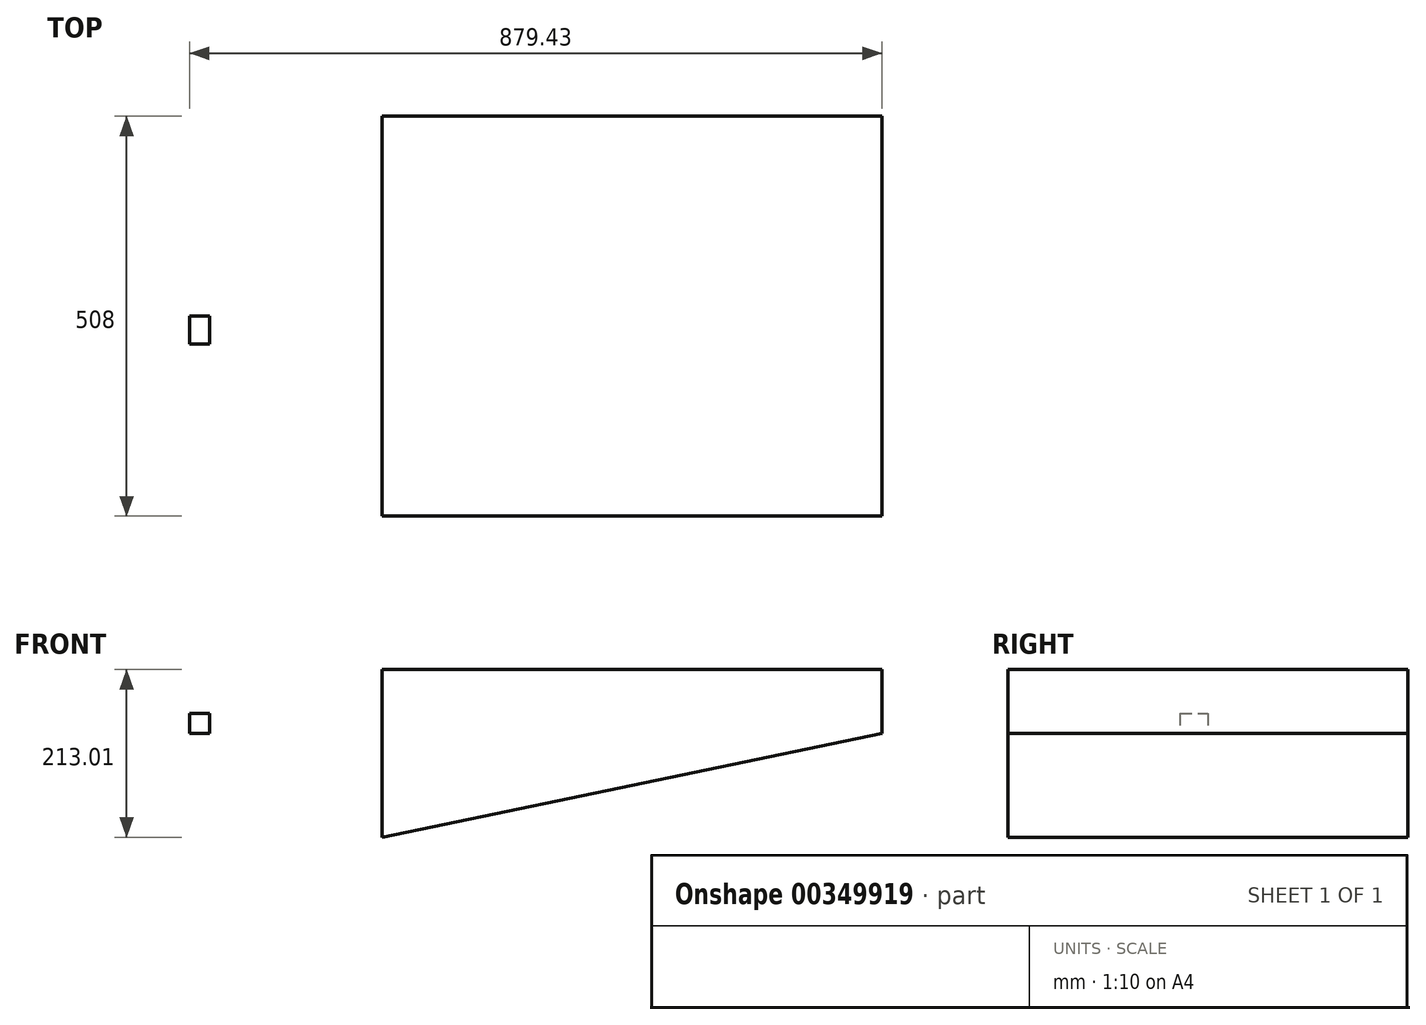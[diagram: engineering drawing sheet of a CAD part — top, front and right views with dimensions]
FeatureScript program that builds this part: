
annotation { "Feature Type Name" : "Feature", "Feature Type Description" : "" }
export const myFeature = defineFeature(function(context is Context, id is Id, definition is map)
    precondition{}
    {
        {
            var Q0;
            Q0=qCreatedBy(makeId("Top.planeOp"),FACE);
            var sketch = newSketch(context, id + "F0", { "sketchPlane" : qUnion([Q0])});
            skLineSegment(sketch, "E0.bottom", {"start": v(317.5, -254) * mm, "end": v(-317.5, -254) * mm});
            skLineSegment(sketch, "E0.top", {"start": v(317.5, 254) * mm, "end": v(-317.5, 254) * mm});
            skLineSegment(sketch, "E0.left", {"start": v(317.5, -254) * mm, "end": v(317.5, 254) * mm});
            skLineSegment(sketch, "E0.right", {"start": v(-317.5, -254) * mm, "end": v(-317.5, 254) * mm});
            skPoint(sketch, "E0.middle", {"position": v(0, 0) * mm});
            skSolve(sketch);
        }
        {
            var Q0;
            Q0 = qSketchRegion(id + "F0", true);
            extrude(context, id + "F1", {"entities" : qUnion([Q0]), "depth" : 81.28 * mm, "offsetDistance" : 25.4 * mm});
        }
        {
            var Q0;
            Q0=makeQuery(id+"F1.opExtrude","SWEPT_FACE",FACE,{"disambiguationData":[OSD([sQuery(id+"F0.wireOp",EDGE,"E0.bottom")])]});
            var sketch = newSketch(context, id + "F2", { "sketchPlane" : qUnion([Q0])});
            skLineSegment(sketch, "E1", {"start": v(-317.5, 26.86) * mm, "end": v(-317.5, -131.73) * mm});
            skLineSegment(sketch, "E2", {"start": v(-317.5, -131.73) * mm, "end": v(317.5, 0) * mm});
            skLineSegment(sketch, "E3", {"start": v(317.5, 0) * mm, "end": v(317.5, 19.8) * mm});
            skLineSegment(sketch, "E4", {"start": v(317.5, 19.8) * mm, "end": v(-317.5, 26.86) * mm});
            skSolve(sketch);
        }
        {
            var Q0;
            Q0 = qSketchRegion(id + "F2", true);
            extrude(context, id + "F3", {"entities" : qUnion([Q0]), "operationType" : NewBodyOperationType.ADD, "oppositeDirection" : true, "depth" : 508 * mm, "offsetDistance" : 25.4 * mm});
        }
        {
            var Q0;
            Q0=qCreatedBy(makeId("Front.planeOp"),FACE);
            var sketch = newSketch(context, id + "F4", { "sketchPlane" : qUnion([Q0])});
            skLineSegment(sketch, "E5.bottom", {"start": v(-561.93, 25.4) * mm, "end": v(-536.53, 25.4) * mm});
            skLineSegment(sketch, "E5.top", {"start": v(-561.93, 0) * mm, "end": v(-536.53, 0) * mm});
            skLineSegment(sketch, "E5.left", {"start": v(-561.93, 25.4) * mm, "end": v(-561.93, 0) * mm});
            skLineSegment(sketch, "E5.right", {"start": v(-536.53, 25.4) * mm, "end": v(-536.53, 0) * mm});
            skSolve(sketch);
        }
        {
            var Q0;
            Q0 = qSketchRegion(id + "F4", true);
            extrude(context, id + "F5", {"entities" : qUnion([Q0]), "depth" : 35.56 * mm, "offsetDistance" : 25.4 * mm});
        }
    });
